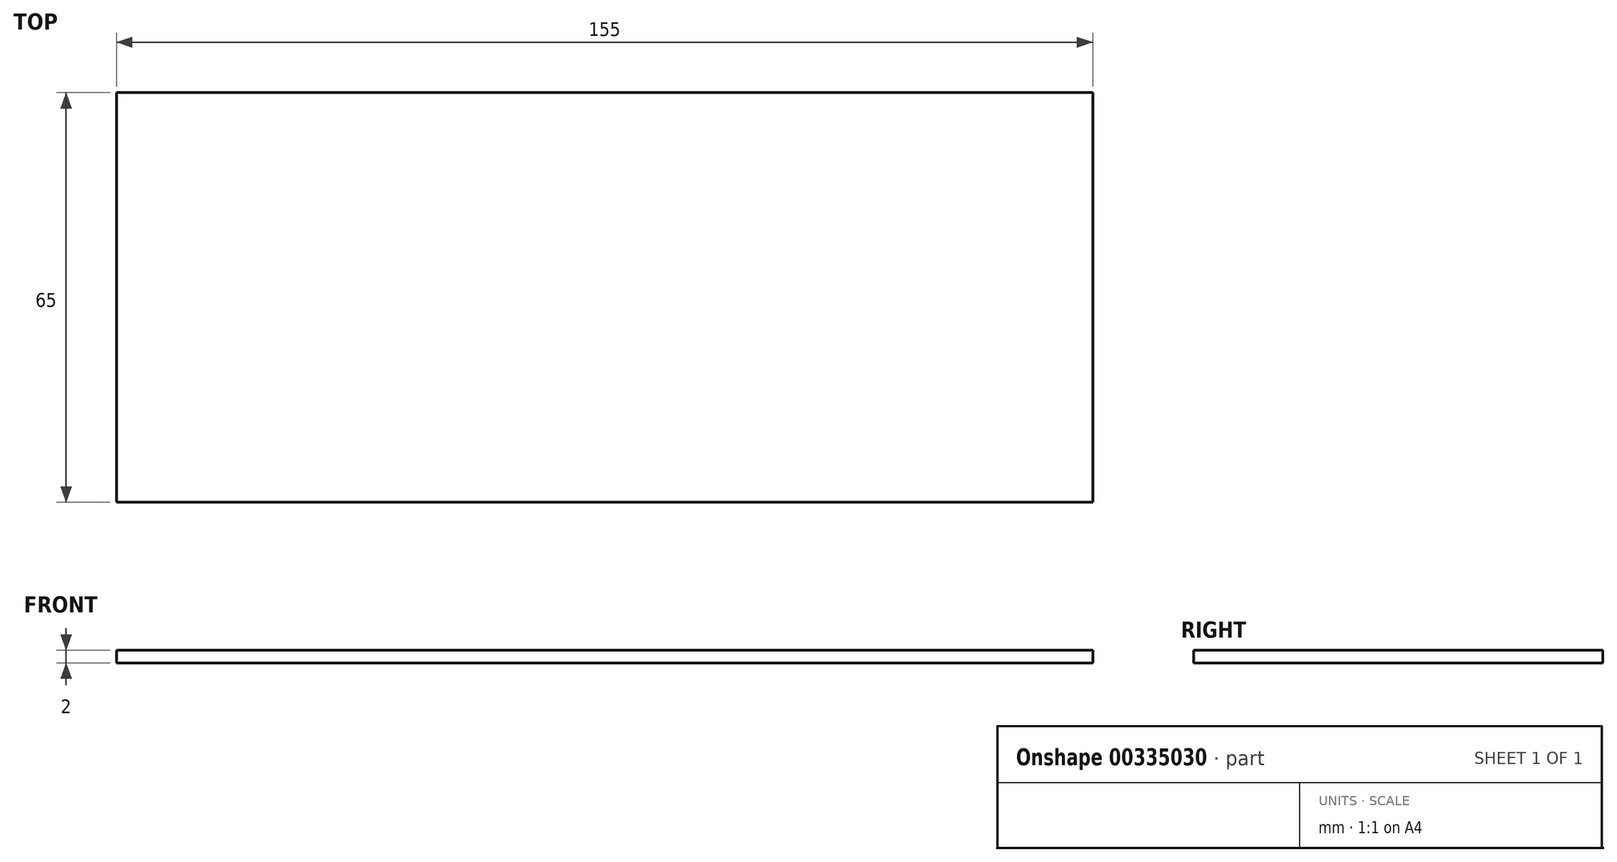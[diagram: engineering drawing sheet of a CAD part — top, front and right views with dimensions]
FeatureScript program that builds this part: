
annotation { "Feature Type Name" : "Feature", "Feature Type Description" : "" }
export const myFeature = defineFeature(function(context is Context, id is Id, definition is map)
    precondition{}
    {
        {
            var Q0;
            Q0=qCreatedBy(makeId("Top.planeOp"),FACE);
            var sketch = newSketch(context, id + "F0", { "sketchPlane" : qUnion([Q0])});
            skLineSegment(sketch, "E0.bottom", {"start": v(77.5, -32.5) * mm, "end": v(-77.5, -32.5) * mm});
            skLineSegment(sketch, "E0.top", {"start": v(77.5, 32.5) * mm, "end": v(-77.5, 32.5) * mm});
            skLineSegment(sketch, "E0.left", {"start": v(77.5, -32.5) * mm, "end": v(77.5, 32.5) * mm});
            skLineSegment(sketch, "E0.right", {"start": v(-77.5, -32.5) * mm, "end": v(-77.5, 32.5) * mm});
            skPoint(sketch, "E0.middle", {"position": v(0, 0) * mm});
            skSolve(sketch);
        }
        {
            var Q0;
            Q0 = qSketchRegion(id + "F0", true);
            extrude(context, id + "F1", {"entities" : qUnion([Q0]), "depth" : 2 * mm});
        }
    });
